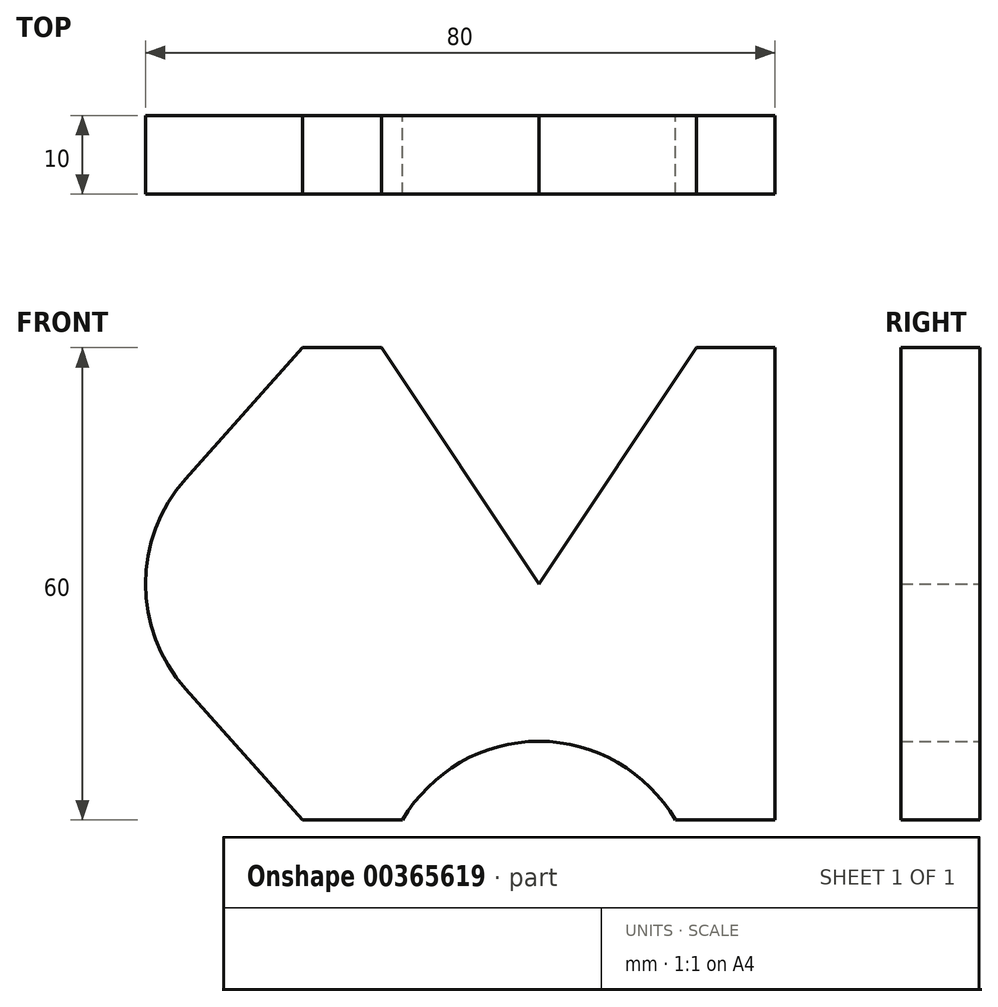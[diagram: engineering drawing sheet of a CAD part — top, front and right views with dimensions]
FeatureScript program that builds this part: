
annotation { "Feature Type Name" : "Feature", "Feature Type Description" : "" }
export const myFeature = defineFeature(function(context is Context, id is Id, definition is map)
    precondition{}
    {
        {
            var Q0;
            Q0=qCreatedBy(makeId("Front.planeOp"),FACE);
            var sketch = newSketch(context, id + "F0", { "sketchPlane" : qUnion([Q0])});
            skLineSegment(sketch, "E0", {"start": v(30, 30) * mm, "end": v(30, -30) * mm});
            skLineSegment(sketch, "E1", {"start": v(30, -30) * mm, "end": v(17.32, -30) * mm});
            skLineSegment(sketch, "E2", {"start": v(-17.32, -30) * mm, "end": v(-30, -30) * mm});
            skLineSegment(sketch, "E3", {"start": v(-30, -30) * mm, "end": v(-44.9, -13.33) * mm});
            skLineSegment(sketch, "E4", {"start": v(-44.9, 13.33) * mm, "end": v(-30, 30) * mm});
            skLineSegment(sketch, "E5", {"start": v(-30, 30) * mm, "end": v(-20, 30) * mm});
            skLineSegment(sketch, "E6", {"start": v(-20, 30) * mm, "end": v(0, 0) * mm});
            skLineSegment(sketch, "E7", {"start": v(0, 0) * mm, "end": v(20, 30) * mm});
            skLineSegment(sketch, "E8", {"start": v(20, 30) * mm, "end": v(30, 30) * mm});
            skArc(sketch, "E9", {"start": v(17.32, -30) * mm, "mid": v(0, -20) * mm, "end": v(-17.32, -30) * mm});
            skArc(sketch, "E10", {"start": v(-44.9, 13.33) * mm, "mid": v(-50, 0) * mm, "end": v(-44.9, -13.33) * mm});
            skSolve(sketch);
        }
        {
            var Q0;
            Q0=makeQuery(id+"F0.imprint","IMPRINT",FACE,{"disambiguationData":[TD([[makeQuery(id+"F0.imprint","IMPRINT",EDGE,{"derivedFrom":sQuery(id+"F0.wireOp",EDGE,"E0")}),-1.0]])]});
            extrude(context, id + "F1", {"entities" : qUnion([Q0]), "depth" : 10 * mm});
        }
    });
